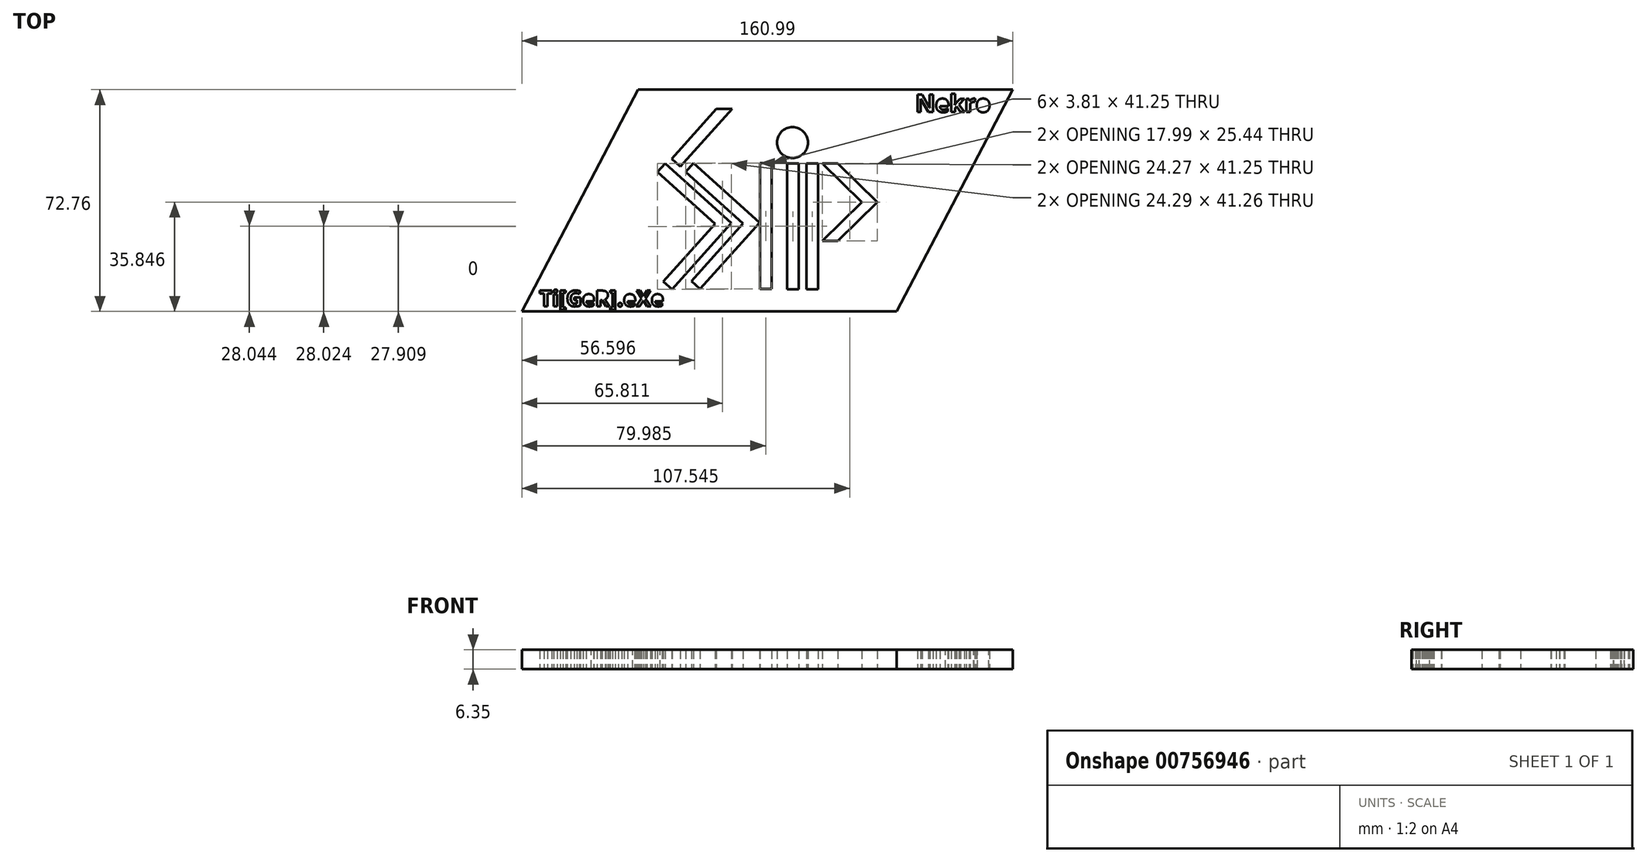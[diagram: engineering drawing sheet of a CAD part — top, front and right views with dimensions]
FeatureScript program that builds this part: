
annotation { "Feature Type Name" : "Feature", "Feature Type Description" : "" }
export const myFeature = defineFeature(function(context is Context, id is Id, definition is map)
    precondition{}
    {
        {
            var Q0;
            Q0=qCreatedBy(makeId("Top.planeOp"),FACE);
            var sketch = newSketch(context, id + "F0", { "sketchPlane" : qUnion([Q0])});
            skLineSegment(sketch, "E0", {"start": v(-49.43, 24.1) * mm, "end": v(-34.76, 40.46) * mm});
            skLineSegment(sketch, "E1", {"start": v(-49.43, 24.1) * mm, "end": v(-46.6, 21.56) * mm});
            skLineSegment(sketch, "E2", {"start": v(-46.6, 21.56) * mm, "end": v(-29.64, 40.46) * mm});
            skLineSegment(sketch, "E3", {"start": v(-29.64, 40.46) * mm, "end": v(-34.76, 40.46) * mm});
            skLineSegment(sketch, "E4", {"start": v(-51.55, 22.6) * mm, "end": v(-32.65, 5.63) * mm});
            skLineSegment(sketch, "E5", {"start": v(-35.2, 2.8) * mm, "end": v(-54.1, 19.76) * mm});
            skLineSegment(sketch, "E6", {"start": v(-54.1, 19.76) * mm, "end": v(-51.55, 22.6) * mm});
            skLineSegment(sketch, "E7", {"start": v(-35.2, 2.8) * mm, "end": v(-52.16, -16.13) * mm});
            skLineSegment(sketch, "E8", {"start": v(-52.16, -16.13) * mm, "end": v(-49.33, -18.67) * mm});
            skLineSegment(sketch, "E9", {"start": v(-49.33, -18.67) * mm, "end": v(-32.37, 0.23) * mm});
            skLineSegment(sketch, "E10", {"start": v(-32.65, 5.63) * mm, "end": v(-29.8, 3.08) * mm});
            skLineSegment(sketch, "E11", {"start": v(-29.8, 3.08) * mm, "end": v(-32.37, 0.23) * mm});
            skLineSegment(sketch, "E12", {"start": v(-42.33, 22.7) * mm, "end": v(-23.44, 5.72) * mm});
            skLineSegment(sketch, "E13", {"start": v(-25.98, 2.89) * mm, "end": v(-44.88, 19.87) * mm});
            skLineSegment(sketch, "E14", {"start": v(-44.88, 19.87) * mm, "end": v(-42.33, 22.7) * mm});
            skLineSegment(sketch, "E15", {"start": v(-25.98, 2.89) * mm, "end": v(-42.96, -16) * mm});
            skLineSegment(sketch, "E16", {"start": v(-42.96, -16) * mm, "end": v(-40.13, -18.55) * mm});
            skLineSegment(sketch, "E17", {"start": v(-40.13, -18.55) * mm, "end": v(-23.15, 0.34) * mm});
            skLineSegment(sketch, "E18", {"start": v(-23.44, 5.72) * mm, "end": v(-20.6, 3.17) * mm});
            skLineSegment(sketch, "E19", {"start": v(-20.6, 3.17) * mm, "end": v(-23.15, 0.34) * mm});
            skLineSegment(sketch, "E20", {"start": v(-20.47, 22.72) * mm, "end": v(-20.47, -18.53) * mm});
            skLineSegment(sketch, "E21", {"start": v(-20.47, -18.53) * mm, "end": v(-16.66, -18.53) * mm});
            skLineSegment(sketch, "E22", {"start": v(-20.47, 22.72) * mm, "end": v(-16.66, 22.72) * mm});
            skLineSegment(sketch, "E23", {"start": v(-16.66, 22.72) * mm, "end": v(-16.66, -18.53) * mm});
            skLineSegment(sketch, "E24", {"start": v(-11.58, 22.64) * mm, "end": v(-11.58, -18.61) * mm});
            skLineSegment(sketch, "E25", {"start": v(-11.58, -18.61) * mm, "end": v(-7.77, -18.61) * mm});
            skLineSegment(sketch, "E26", {"start": v(-11.58, 22.64) * mm, "end": v(-7.77, 22.64) * mm});
            skLineSegment(sketch, "E27", {"start": v(-7.77, 22.64) * mm, "end": v(-7.77, -18.61) * mm});
            skLineSegment(sketch, "E28", {"start": v(-5.23, 22.62) * mm, "end": v(-5.23, -18.64) * mm});
            skLineSegment(sketch, "E29", {"start": v(-5.23, -18.64) * mm, "end": v(-1.42, -18.64) * mm});
            skLineSegment(sketch, "E30", {"start": v(-5.23, 22.62) * mm, "end": v(-1.42, 22.62) * mm});
            skLineSegment(sketch, "E31", {"start": v(-1.42, 22.62) * mm, "end": v(-1.42, -18.64) * mm});
            skCircle(sketch, "E32", {"center": v(-9.8, 29.44) * mm, "radius": 5.08 * mm});
            skLineSegment(sketch, "E33", {"start": v(0, 22.62) * mm, "end": v(5.08, 22.62) * mm});
            skLineSegment(sketch, "E34", {"start": v(5.08, -2.83) * mm, "end": v(0, -2.83) * mm});
            skLineSegment(sketch, "E35", {"start": v(12.91, 9.9) * mm, "end": v(0, 22.62) * mm});
            skLineSegment(sketch, "E36", {"start": v(0, -2.83) * mm, "end": v(12.91, 9.9) * mm});
            skLineSegment(sketch, "E37", {"start": v(5.08, -2.83) * mm, "end": v(18, 9.9) * mm});
            skLineSegment(sketch, "E38", {"start": v(18, 9.9) * mm, "end": v(5.08, 22.62) * mm});
            skLineSegment(sketch, "E39", {"start": v(-60.45, 46.81) * mm, "end": v(24.34, 46.81) * mm});
            skLineSegment(sketch, "E40", {"start": v(24.34, -25.95) * mm, "end": v(62.44, 46.81) * mm});
            skLineSegment(sketch, "E41", {"start": v(62.44, 46.81) * mm, "end": v(24.34, 46.81) * mm});
            skLineSegment(sketch, "E42", {"start": v(-60.45, 46.81) * mm, "end": v(-98.55, -25.95) * mm});
            skText(sketch, "E43", { "text": "Nekro", "fontName": "OpenSans-Bold.ttf"});
            skText(sketch, "E44", { "text": "Ti[GeR].eXe", "fontName": "OpenSans-Bold.ttf"});
            skLineSegment(sketch, "E45", {"start": v(-98.55, -25.95) * mm, "end": v(24.34, -25.95) * mm});
            const initialGuessF0  = {"E43": [0.03051, 0.03946, 1, 0, 0.00575], "E44": [-0.09283, -0.02425, 1, 0, 0.0052]};
            skSetInitialGuess(sketch, initialGuessF0);
            skSolve(sketch);
        }
        {
            var Q0;
            Q0=makeQuery(id+"F0.imprint","IMPRINT",FACE,{"disambiguationData":[TD([[makeQuery(id+"F0.imprint","IMPRINT",EDGE,{"derivedFrom":sQuery(id+"F0.wireOp",EDGE,"E0")}),1.0]])]});
            extrude(context, id + "F1", {"entities" : qUnion([Q0]), "depth" : 6.35 * mm, "offsetDistance" : 25.4 * mm});
        }
    });
